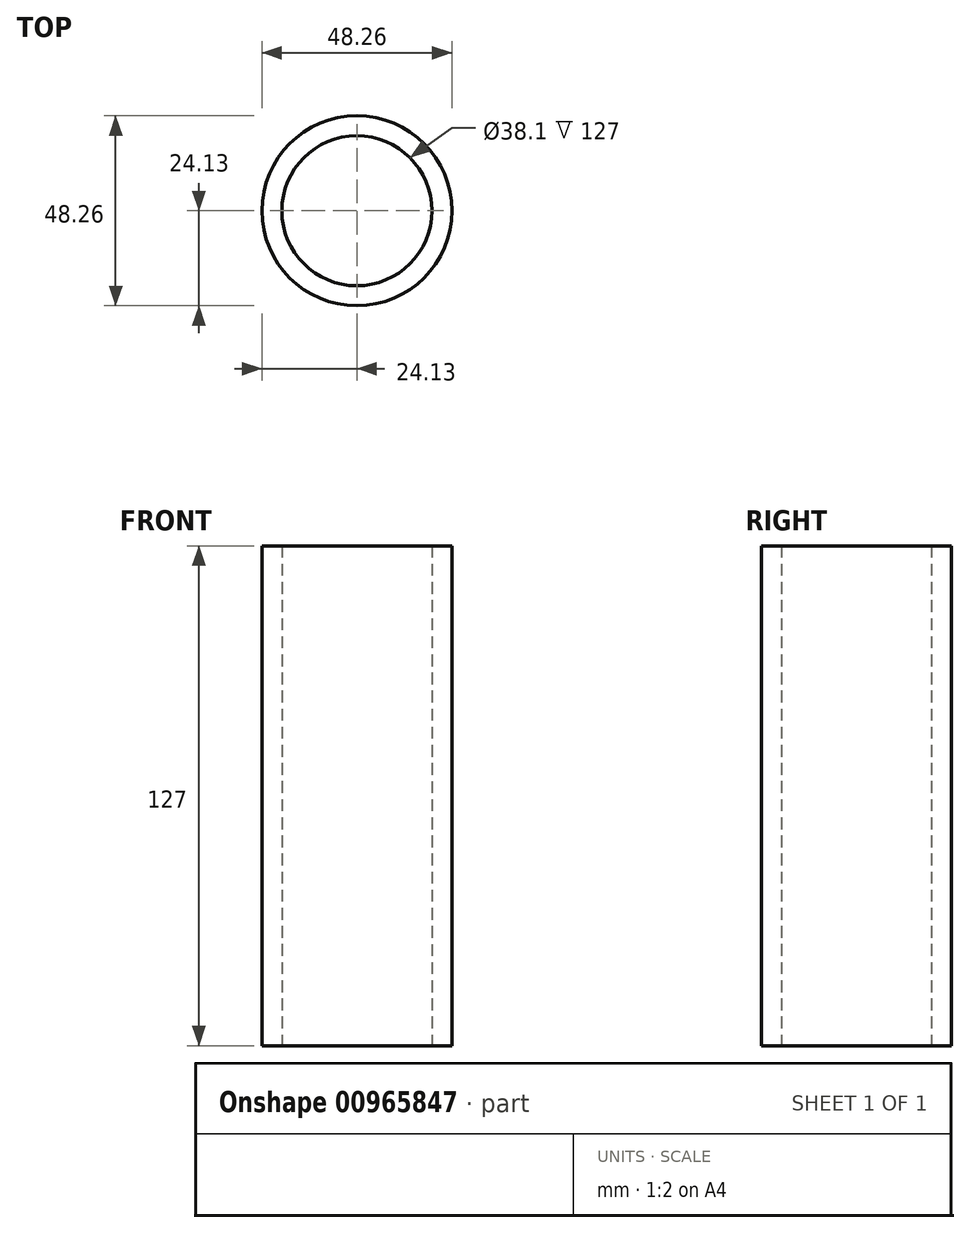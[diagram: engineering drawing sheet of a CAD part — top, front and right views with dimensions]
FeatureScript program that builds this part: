
annotation { "Feature Type Name" : "Feature", "Feature Type Description" : "" }
export const myFeature = defineFeature(function(context is Context, id is Id, definition is map)
    precondition{}
    {
        {
            var Q0;
            Q0=qCreatedBy(makeId("Top.planeOp"),FACE);
            var sketch = newSketch(context, id + "F0", { "sketchPlane" : qUnion([Q0])});
            skCircle(sketch, "E0", {"center": v(0, 0) * mm, "radius": 24.13 * mm});
            skCircle(sketch, "E1", {"center": v(0, 0) * mm, "radius": 19.05 * mm});
            skSolve(sketch);
        }
        {
            var Q0;
            Q0=makeQuery(id+"F0.imprint","IMPRINT",FACE,{"disambiguationData":[TD([[makeQuery(id+"F0.imprint","IMPRINT",EDGE,{"derivedFrom":sQuery(id+"F0.wireOp",EDGE,"E0")}),1.0]])]});
            extrude(context, id + "F1", {"entities" : qUnion([Q0]), "depth" : 127 * mm, "offsetDistance" : 25.4 * mm});
        }
    });
